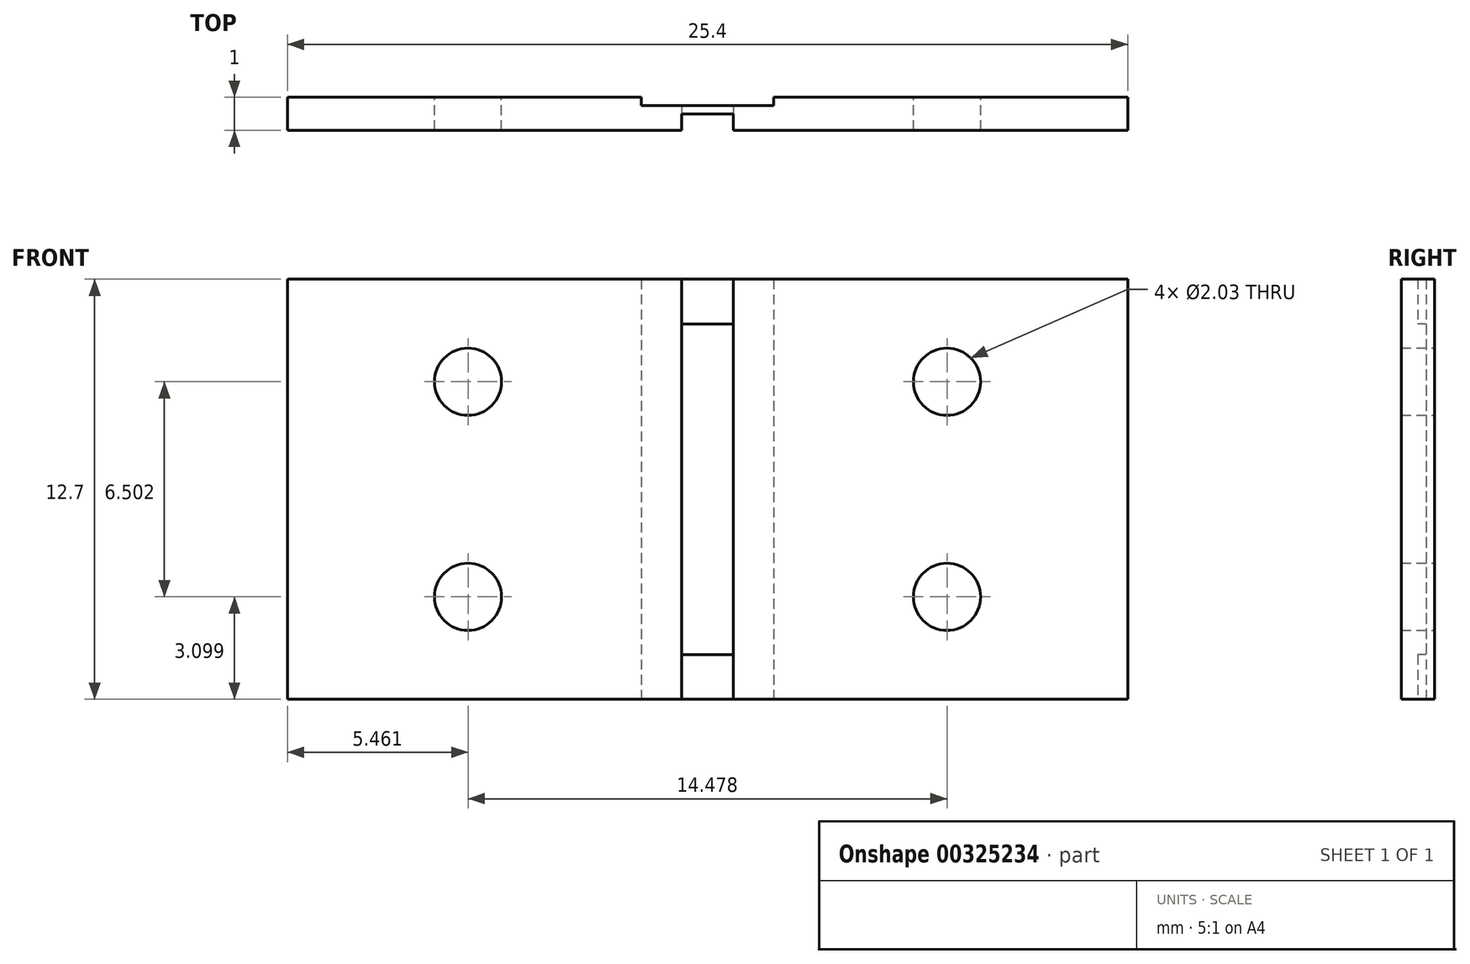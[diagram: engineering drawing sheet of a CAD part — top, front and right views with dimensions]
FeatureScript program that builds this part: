
annotation { "Feature Type Name" : "Feature", "Feature Type Description" : "" }
export const myFeature = defineFeature(function(context is Context, id is Id, definition is map)
    precondition{}
    {
        {
            var Q0;
            Q0=qCreatedBy(makeId("Front.planeOp"),FACE);
            var sketch = newSketch(context, id + "F0", { "sketchPlane" : qUnion([Q0])});
            skLineSegment(sketch, "E0.bottom", {"start": v(12.7, -6.35) * mm, "end": v(-12.7, -6.35) * mm});
            skLineSegment(sketch, "E0.top", {"start": v(12.7, 6.35) * mm, "end": v(-12.7, 6.35) * mm});
            skLineSegment(sketch, "E0.left", {"start": v(12.7, -6.35) * mm, "end": v(12.7, 6.35) * mm});
            skLineSegment(sketch, "E0.right", {"start": v(-12.7, -6.35) * mm, "end": v(-12.7, 6.35) * mm});
            skPoint(sketch, "E0.middle", {"position": v(0, 0) * mm});
            skSolve(sketch);
        }
        {
            var Q0;
            Q0=makeQuery(id+"F0.imprint","IMPRINT",FACE,{"disambiguationData":[TD([[makeQuery(id+"F0.imprint","IMPRINT",EDGE,{"derivedFrom":sQuery(id+"F0.wireOp",EDGE,"E0.bottom")}),-1.0]])]});
            extrude(context, id + "F1", {"entities" : qUnion([Q0]), "depth" : 1 * mm});
        }
        {
            var Q0;
            Q0=qCreatedBy(makeId("Front.planeOp"),FACE);
            var sketch = newSketch(context, id + "F2", { "sketchPlane" : qUnion([Q0])});
            skLineSegment(sketch, "E1.bottom", {"start": v(-7.24, 3.25) * mm, "end": v(7.24, 3.25) * mm});
            skLineSegment(sketch, "E1.top", {"start": v(-7.24, -3.25) * mm, "end": v(7.24, -3.25) * mm});
            skLineSegment(sketch, "E1.left", {"start": v(-7.24, 3.25) * mm, "end": v(-7.24, -3.25) * mm});
            skLineSegment(sketch, "E1.right", {"start": v(7.24, 3.25) * mm, "end": v(7.24, -3.25) * mm});
            skPoint(sketch, "E1.middle", {"position": v(0, 0) * mm});
            skSolve(sketch);
        }
        {
            var Q0;
            Q0=sQuery(id+"F2.wireOp",VERTEX,"E1.left.start");
            var Q1;
            Q1=sQuery(id+"F2.wireOp",VERTEX,"E1.right.start");
            var Q2;
            Q2=sQuery(id+"F2.wireOp",VERTEX,"E1.top.end");
            var Q3;
            Q3=sQuery(id+"F2.wireOp",VERTEX,"E1.left.end");
            var Q4;
            Q4=makeQuery(id+"F1.opExtrude","SWEPT_BODY",BODY,{"disambiguationData":[OSD([sQuery(id+"F0.wireOp",EDGE,"E0.bottom"),sQuery(id+"F0.wireOp",EDGE,"E0.top"),sQuery(id+"F0.wireOp",EDGE,"E0.left"),sQuery(id+"F0.wireOp",EDGE,"E0.right")])]});
            hole(context, id + "F3", {"style" : HoleStyle.SIMPLE, "endStyle" : HoleEndStyle.THROUGH, "oppositeDirection" : true, "holeDiameter" : 2.03 * mm, "tappedDepth" : 12.7 * mm, "tapClearance" : 3, "startFromSketch" : true, "locations" : qUnion([Q0, Q1, Q2, Q3]), "scope" : qUnion([Q4])});
        }
        {
            var Q0;
            Q0=qCreatedBy(makeId("Front.planeOp"),FACE);
            var sketch = newSketch(context, id + "F4", { "sketchPlane" : qUnion([Q0])});
            skLineSegment(sketch, "E2.bottom", {"start": v(2, 6.35) * mm, "end": v(-2, 6.35) * mm});
            skLineSegment(sketch, "E2.top", {"start": v(2, -6.35) * mm, "end": v(-2, -6.35) * mm});
            skLineSegment(sketch, "E2.left", {"start": v(2, 6.35) * mm, "end": v(2, -6.35) * mm});
            skLineSegment(sketch, "E2.right", {"start": v(-2, 6.35) * mm, "end": v(-2, -6.35) * mm});
            skPoint(sketch, "E2.middle", {"position": v(0, 0) * mm});
            skSolve(sketch);
        }
        {
            var Q0;
            Q0=makeQuery(id+"F4.imprint","IMPRINT",FACE,{"disambiguationData":[TD([[makeQuery(id+"F4.imprint","IMPRINT",EDGE,{"derivedFrom":sQuery(id+"F4.wireOp",EDGE,"E2.bottom")}),1.0]])]});
            extrude(context, id + "F5", {"entities" : qUnion([Q0]), "operationType" : NewBodyOperationType.REMOVE, "depth" : 0.25 * mm});
        }
        {
            var Q0;
            Q0=makeQuery(id+"F1.opExtrude","CAP_FACE",FACE,{"disambiguationData":[OSD([sQuery(id+"F0.wireOp",EDGE,"E0.bottom"),sQuery(id+"F0.wireOp",EDGE,"E0.top"),sQuery(id+"F0.wireOp",EDGE,"E0.left"),sQuery(id+"F0.wireOp",EDGE,"E0.right")])],"isStart":false});
            var sketch = newSketch(context, id + "F6", { "sketchPlane" : qUnion([Q0])});
            skLineSegment(sketch, "E3.bottom", {"start": v(0.78, 6.35) * mm, "end": v(-0.77, 6.35) * mm});
            skLineSegment(sketch, "E3.top", {"start": v(0.78, -6.35) * mm, "end": v(-0.78, -6.35) * mm});
            skLineSegment(sketch, "E3.left", {"start": v(0.78, 6.35) * mm, "end": v(0.78, -6.35) * mm});
            skLineSegment(sketch, "E3.right", {"start": v(-0.77, 6.35) * mm, "end": v(-0.78, -6.35) * mm});
            skPoint(sketch, "E3.middle", {"position": v(0, 0) * mm});
            skSolve(sketch);
        }
        {
            var Q0;
            Q0=makeQuery(id+"F6.imprint","IMPRINT",FACE,{"disambiguationData":[TD([[makeQuery(id+"F6.imprint","IMPRINT",EDGE,{"derivedFrom":sQuery(id+"F6.wireOp",EDGE,"E3.bottom")}),1.0]])]});
            extrude(context, id + "F7", {"entities" : qUnion([Q0]), "operationType" : NewBodyOperationType.REMOVE, "oppositeDirection" : true, "depth" : .5 * mm});
        }
        {
            var Q0;
            Q0=makeQuery(id+"F7.boolean.opBoolean","COPY",FACE,{"derivedFrom":makeQuery(id+"F7.opExtrude","CAP_FACE",FACE,{"disambiguationData":[OSD([sQuery(id+"F6.wireOp",EDGE,"E3.bottom"),sQuery(id+"F6.wireOp",EDGE,"E3.top"),sQuery(id+"F6.wireOp",EDGE,"E3.left"),sQuery(id+"F6.wireOp",EDGE,"E3.right")])],"isStart":false})});
            var sketch = newSketch(context, id + "F8", { "sketchPlane" : qUnion([Q0])});
            skLineSegment(sketch, "E4.bottom", {"start": v(0.78, 5) * mm, "end": v(-0.78, 5) * mm});
            skLineSegment(sketch, "E4.top", {"start": v(0.78, -5) * mm, "end": v(-0.78, -5) * mm});
            skLineSegment(sketch, "E4.left", {"start": v(0.78, 5) * mm, "end": v(0.78, -5) * mm});
            skLineSegment(sketch, "E4.right", {"start": v(-0.78, 5) * mm, "end": v(-0.78, -5) * mm});
            skPoint(sketch, "E4.middle", {"position": v(0, 0) * mm});
            skSolve(sketch);
        }
        {
            var Q0;
            Q0=makeQuery(id+"F8.imprint","IMPRINT",FACE,{"disambiguationData":[TD([[makeQuery(id+"F8.imprint","IMPRINT",EDGE,{"derivedFrom":sQuery(id+"F8.wireOp",EDGE,"E4.bottom")}),1.0]])]});
            extrude(context, id + "F9", {"entities" : qUnion([Q0]), "operationType" : NewBodyOperationType.REMOVE, "oppositeDirection" : true, "depth" : .25 * mm});
        }
    });
